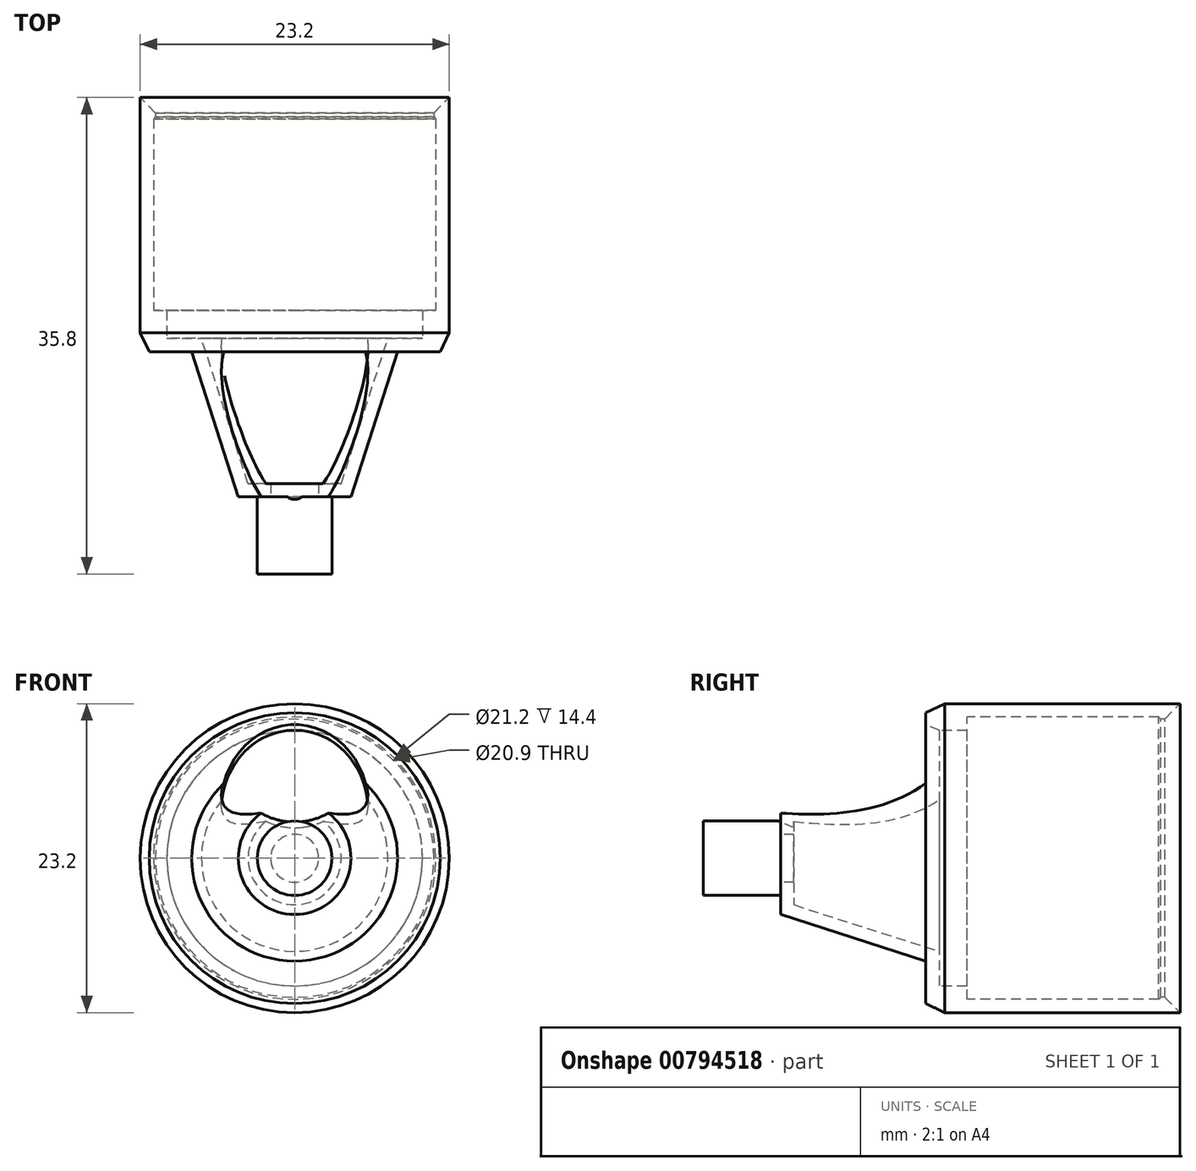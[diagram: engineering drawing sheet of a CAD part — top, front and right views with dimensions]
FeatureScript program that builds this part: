
annotation { "Feature Type Name" : "Feature", "Feature Type Description" : "" }
export const myFeature = defineFeature(function(context is Context, id is Id, definition is map)
    precondition{}
    {
        {
            var Q0;
            Q0=qCreatedBy(makeId("Right.planeOp"),FACE);
            var sketch = newSketch(context, id + "F0", { "sketchPlane" : qUnion([Q0])});
            skCircle(sketch, "E0", {"center": v(0, 0) * mm, "radius": 10.55 * mm});
            skCircle(sketch, "E1.0", {"center": v(0, 0) * mm, "radius": 11.35 * mm});
            skCircle(sketch, "E2", {"center": v(23, 0) * mm, "radius": 9.65 * mm});
            skCircle(sketch, "E3.0", {"center": v(23, 0) * mm, "radius": 10.45 * mm});
            skArc(sketch, "E4", {"start": v(8.12, -10.4) * mm, "mid": v(12.5, -30.55) * mm, "end": v(16.88, -10.4) * mm});
            skLineSegment(sketch, "E5", {"start": v(8.12, -10.4) * mm, "end": v(16.88, -10.4) * mm});
            skLineSegment(sketch, "E6", {"start": v(2.23, -30.55) * mm, "end": v(24.48, -30.55) * mm, "construction": true});
            skArc(sketch, "E7.0", {"start": v(7.95, -9.6) * mm, "mid": v(12.5, -31.35) * mm, "end": v(17.05, -9.6) * mm});
            skLineSegment(sketch, "E7.1", {"start": v(7.95, -9.6) * mm, "end": v(17.05, -9.6) * mm});
            skCircle(sketch, "E8", {"center": v(12.5, 16) * mm, "radius": 7.1 * mm});
            skCircle(sketch, "E9.0", {"center": v(12.5, 16) * mm, "radius": 7.9 * mm});
            skLineSegment(sketch, "E10", {"start": v(73.65, 1.8) * mm, "end": v(73.65, 3.5) * mm});
            skLineSegment(sketch, "E11", {"start": v(73.65, 3.5) * mm, "end": v(84.55, 7) * mm});
            skLineSegment(sketch, "E12", {"start": v(84.55, 7) * mm, "end": v(84.55, 9.6) * mm});
            skLineSegment(sketch, "E13", {"start": v(84.55, 9.6) * mm, "end": v(86.65, 9.6) * mm});
            skLineSegment(sketch, "E14", {"start": v(86.65, 9.6) * mm, "end": v(86.65, 10.6) * mm});
            skLineSegment(sketch, "E15", {"start": v(86.65, 10.6) * mm, "end": v(101.05, 10.6) * mm});
            skLineSegment(sketch, "E16", {"start": v(101.05, 10.6) * mm, "end": v(101.2, 10.45) * mm});
            skLineSegment(sketch, "E17.0", {"start": v(84.97, 11.6) * mm, "end": v(102.65, 11.6) * mm});
            skLineSegment(sketch, "E17.3", {"start": v(83.55, 7.73) * mm, "end": v(83.55, 10.92) * mm});
            skLineSegment(sketch, "E17.4", {"start": v(66.85, 0) * mm, "end": v(66.85, 2.8) * mm});
            skLineSegment(sketch, "E17.5", {"start": v(66.85, 2.8) * mm, "end": v(72.65, 2.8) * mm});
            skLineSegment(sketch, "E17.6", {"start": v(72.65, 2.8) * mm, "end": v(72.65, 4.23) * mm});
            skLineSegment(sketch, "E17.7", {"start": v(72.65, 4.23) * mm, "end": v(83.55, 7.73) * mm});
            skLineSegment(sketch, "E18", {"start": v(66.85, 0) * mm, "end": v(72.65, 0) * mm});
            skLineSegment(sketch, "E19", {"start": v(101.2, 10.45) * mm, "end": v(101.5, 10.45) * mm});
            skLineSegment(sketch, "E20", {"start": v(83.55, 10.92) * mm, "end": v(84.97, 11.6) * mm});
            skLineSegment(sketch, "E21", {"start": v(101.5, 10.45) * mm, "end": v(102.65, 11.6) * mm});
            skLineSegment(sketch, "E22", {"start": v(73.65, 1.8) * mm, "end": v(72.65, 1.8) * mm});
            skLineSegment(sketch, "E23", {"start": v(72.65, 1.8) * mm, "end": v(72.65, 0) * mm});
            skSolve(sketch);
        }
        {
            var Q0;
            Q0=makeQuery(id+"F0.imprint","IMPRINT",FACE,{"disambiguationData":[TD([[makeQuery(id+"F0.imprint","IMPRINT",EDGE,{"derivedFrom":sQuery(id+"F0.wireOp",EDGE,"E10")}),1.0]])]});
            var Q1;
            Q1=sQuery(id+"F0.wireOp",EDGE,"E18");
            revolve(context, id + "F1", {"surfaceOperationType" : NewSurfaceOperationType.NEW, "entities" : qUnion([Q0]), "axis" : qUnion([Q1]), "revolveType" : RevolveType.FULL});
        }
        {
            var Q0;
            Q0=qCreatedBy(makeId("Top.planeOp"),FACE);
            var sketch = newSketch(context, id + "F2", { "sketchPlane" : qUnion([Q0])});
            skLineSegment(sketch, "E24", {"start": v(-50.94, 72.65) * mm, "end": v(53.1, 72.65) * mm, "construction": true});
            skSolve(sketch);
        }
        {
            var Q0;
            Q0=qCreatedBy(makeId("Front.planeOp"),FACE);
            var Q1;
            Q1=sQuery(id+"F2.wireOp",EDGE,"E24");
            cPlane(context, id + "F3", {"entities" : qUnion([Q0, Q1]), "cplaneType" : CPlaneType.LINE_ANGLE, "offset" : 25 * mm, "angle" : 23 * degree, "oppositeDirection" : true, "width" : 150 * mm, "height" : 150 * mm});
        }
        {
            var Q0;
            Q0=qCreatedBy(id+"F3.planeOp",FACE);
            var sketch = newSketch(context, id + "F4", { "sketchPlane" : qUnion([Q0])});
            skCircle(sketch, "E25", {"center": v(0, 36.39) * mm, "radius": 5.5 * mm});
            skLineSegment(sketch, "E26", {"start": v(0, 45.73) * mm, "end": v(0, 28.39) * mm, "construction": true});
            skSolve(sketch);
        }
        {
            var Q0;
            Q0 = qSketchRegion(id + "F4", true);
            var Q1;
            Q1=makeQuery(id+"F1.opRevolve","SWEPT_FACE",FACE,{"disambiguationData":[OSD([sQuery(id+"F0.wireOp",EDGE,"E10")])]});
            extrude(context, id + "F5", {"entities" : qUnion([Q0]), "operationType" : NewBodyOperationType.REMOVE, "endBound" : BoundingType.SYMMETRIC, "depth" : 91.66 * mm, "offsetDistance" : 25 * mm});
        }
        {
            var Q0;
            Q0=makeQuery(id+"F1.opRevolve","SWEPT_FACE",FACE,{"disambiguationData":[OSD([sQuery(id+"F0.wireOp",EDGE,"E10")])]});
            cPlane(context, id + "F6", {"entities" : qUnion([Q0]), "cplaneType" : CPlaneType.OFFSET, "offset" : 0 * mm, "width" : 150 * mm, "height" : 150 * mm});
        }
    });
